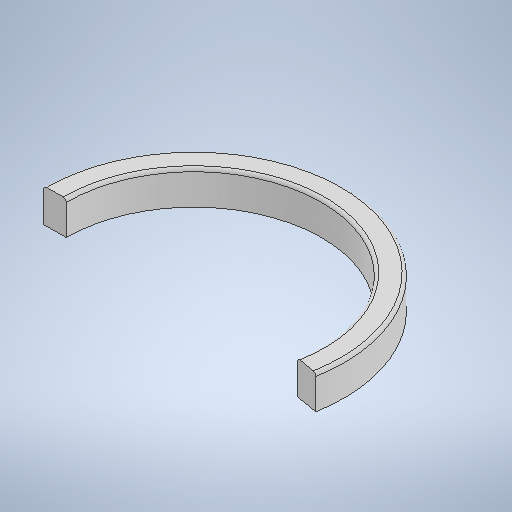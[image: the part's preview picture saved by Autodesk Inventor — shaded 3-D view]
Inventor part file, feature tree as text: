
AUTODESK INVENTOR PART (.ipt)
format: ipt  version: 2025 (Build 290162000, 162)  size: 254,976 bytes
history: native  units: in
note: dims shown in document units (in); Inventor stores cm internally (conversion verified against a paired STEP export)
features: revolve x1, sketch x1
ambient origin geometry x8: Origin, YZ Plane, XZ Plane, XY Plane, X Axis, Y Axis, Z Axis, Center Point
bodies: Solid1 (feature_tree)
feature tree (2):
  revolve  "Revolution1"  Angle=90.0deg
  sketch  "Sketch1"  dims[d0=0.8583in d1=90.0deg d2=0.2894in d3=0.5787in d4=0.0787in d5=3.5433in d6=1.3056in d7=0.0in]
